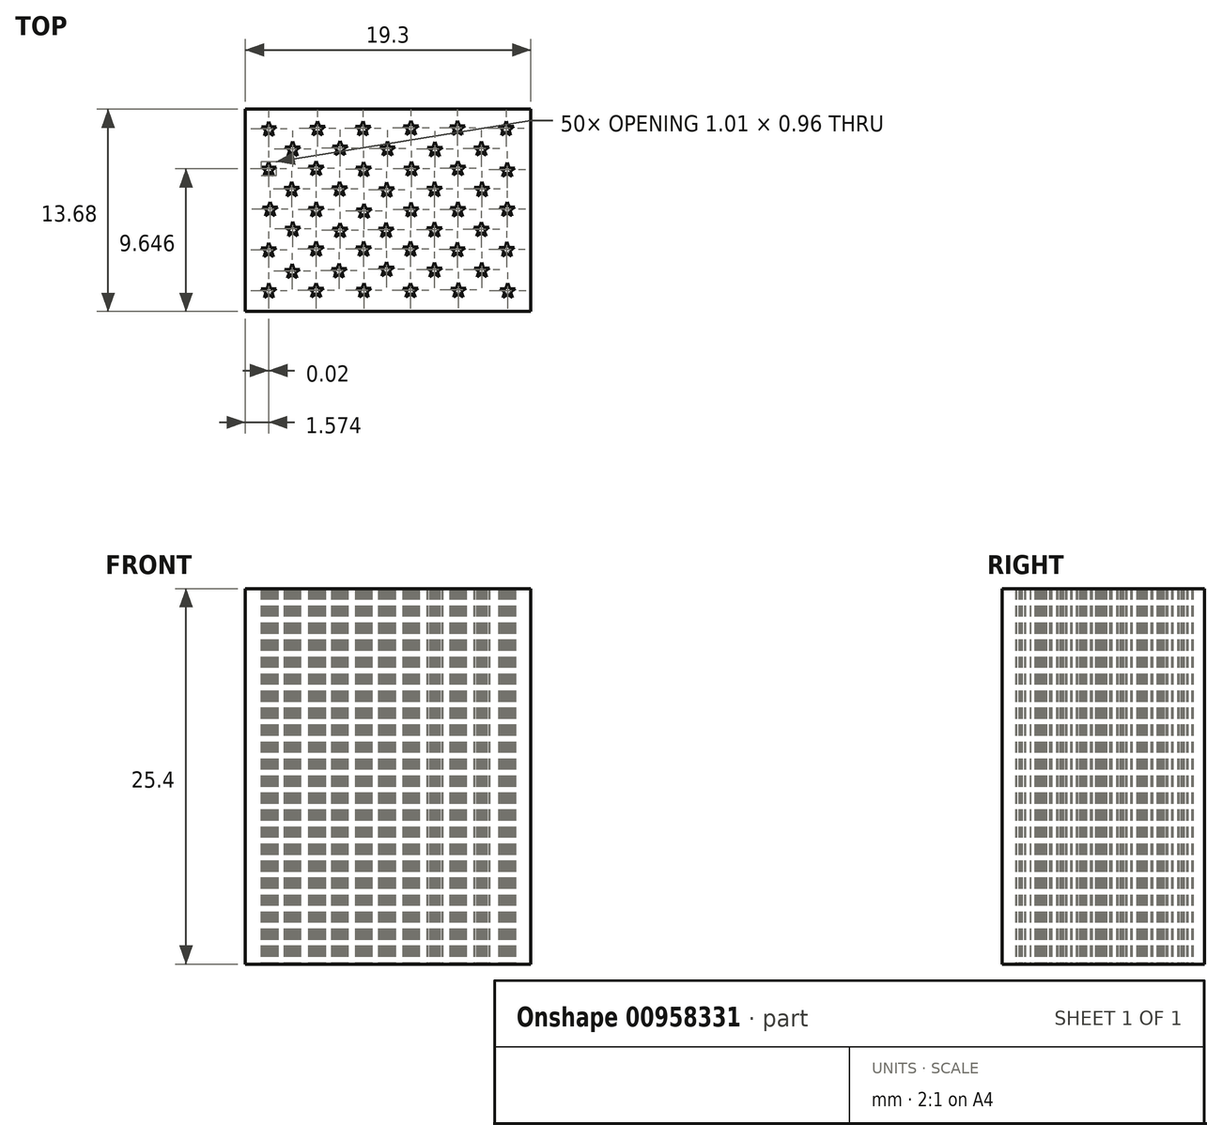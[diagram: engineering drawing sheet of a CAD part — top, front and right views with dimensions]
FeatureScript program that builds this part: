
annotation { "Feature Type Name" : "Feature", "Feature Type Description" : "" }
export const myFeature = defineFeature(function(context is Context, id is Id, definition is map)
    precondition{}
    {
        {
            var Q0;
            Q0=qCreatedBy(makeId("Top.planeOp"),FACE);
            var sketch = newSketch(context, id + "F0", { "sketchPlane" : qUnion([Q0])});
            skLineSegment(sketch, "E0", {"start": v(0, 0) * mm, "end": v(-48.26, 0) * mm});
            skLineSegment(sketch, "E1", {"start": v(-48.26, 0) * mm, "end": v(-48.26, 25.4) * mm});
            skLineSegment(sketch, "E2", {"start": v(-48.26, 25.4) * mm, "end": v(0, 25.4) * mm});
            skLineSegment(sketch, "E3", {"start": v(0, 25.4) * mm, "end": v(0, 0) * mm});
            skLineSegment(sketch, "E4", {"start": v(-49.37, -10.84) * mm, "end": v(-48.47, -27.32) * mm});
            skLineSegment(sketch, "E5", {"start": v(-49.37, -10.84) * mm, "end": v(-38.96, -23.65) * mm});
            skLineSegment(sketch, "E6", {"start": v(-23.56, -17.7) * mm, "end": v(-38.96, -23.65) * mm});
            skLineSegment(sketch, "E7", {"start": v(-47.03, -53.99) * mm, "end": v(-38.06, -40.13) * mm});
            skLineSegment(sketch, "E8.trimOffspring", {"start": v(-32.52, -31.56) * mm, "end": v(-22.11, -44.37) * mm});
            skLineSegment(sketch, "E9.trimOffspring", {"start": v(-32.52, -31.56) * mm, "end": v(-23.56, -17.7) * mm});
            skLineSegment(sketch, "E10.trimOffspring", {"start": v(-38.06, -40.13) * mm, "end": v(-22.11, -44.37) * mm});
            skLineSegment(sketch, "E11.0", {"start": v(-28.96, 23.45) * mm, "end": v(0, 23.45) * mm});
            skLineSegment(sketch, "E12.0", {"start": v(-28.96, 21.5) * mm, "end": v(0, 21.5) * mm});
            skLineSegment(sketch, "E13.0", {"start": v(-28.96, 19.54) * mm, "end": v(0, 19.54) * mm});
            skLineSegment(sketch, "E14.0", {"start": v(-28.96, 13.68) * mm, "end": v(0, 13.68) * mm});
            skLineSegment(sketch, "E15.0", {"start": v(-48.26, 11.72) * mm, "end": v(0, 11.72) * mm});
            skLineSegment(sketch, "E16.0", {"start": v(-48.26, 9.76) * mm, "end": v(0, 9.76) * mm});
            skLineSegment(sketch, "E17.0", {"start": v(-48.26, 7.8) * mm, "end": v(0, 7.8) * mm});
            skLineSegment(sketch, "E18.0", {"start": v(-48.26, 5.85) * mm, "end": v(0, 5.85) * mm});
            skLineSegment(sketch, "E19.0", {"start": v(-48.26, 3.9) * mm, "end": v(0, 3.9) * mm});
            skLineSegment(sketch, "E20.0", {"start": v(-48.26, 1.94) * mm, "end": v(0, 1.94) * mm});
            skLineSegment(sketch, "E21.0", {"start": v(-48.26, 11.7) * mm, "end": v(0, 11.7) * mm});
            skLineSegment(sketch, "E22.0", {"start": v(-46.94, 24.03) * mm, "end": v(-46.38, 24.03) * mm});
            skLineSegment(sketch, "E23", {"start": v(-47.17, 24.2) * mm, "end": v(-46.85, 23.97) * mm});
            skLineSegment(sketch, "E24", {"start": v(-46.97, 23.6) * mm, "end": v(-46.85, 23.97) * mm});
            skLineSegment(sketch, "E25", {"start": v(-46.15, 24.2) * mm, "end": v(-46.47, 23.97) * mm});
            skLineSegment(sketch, "E26", {"start": v(-46.66, 24.56) * mm, "end": v(-46.54, 24.2) * mm});
            skLineSegment(sketch, "E27", {"start": v(-47.17, 24.2) * mm, "end": v(-46.78, 24.2) * mm});
            skLineSegment(sketch, "E28.trimOffspring", {"start": v(-46.66, 23.82) * mm, "end": v(-46.97, 23.6) * mm});
            skLineSegment(sketch, "E29.trimOffspring", {"start": v(-46.47, 23.97) * mm, "end": v(-46.35, 23.6) * mm});
            skLineSegment(sketch, "E30.trimOffspring", {"start": v(-46.54, 24.2) * mm, "end": v(-46.15, 24.2) * mm});
            skLineSegment(sketch, "E31.trimOffspring", {"start": v(-46.66, 23.82) * mm, "end": v(-46.35, 23.6) * mm});
            skLineSegment(sketch, "E32.trimOffspring", {"start": v(-46.78, 24.2) * mm, "end": v(-46.66, 24.56) * mm});
            skLineSegment(sketch, "E33", {"start": v(-45.57, 22.83) * mm, "end": v(-45.25, 22.6) * mm});
            skLineSegment(sketch, "E34", {"start": v(-45.37, 22.24) * mm, "end": v(-45.25, 22.6) * mm});
            skLineSegment(sketch, "E35", {"start": v(-44.55, 22.83) * mm, "end": v(-44.87, 22.6) * mm});
            skLineSegment(sketch, "E36", {"start": v(-45.06, 23.2) * mm, "end": v(-44.94, 22.83) * mm});
            skLineSegment(sketch, "E37", {"start": v(-45.57, 22.83) * mm, "end": v(-45.18, 22.83) * mm});
            skLineSegment(sketch, "E38.trimOffspring", {"start": v(-45.06, 22.46) * mm, "end": v(-45.37, 22.24) * mm});
            skLineSegment(sketch, "E39.trimOffspring", {"start": v(-44.87, 22.6) * mm, "end": v(-44.75, 22.24) * mm});
            skLineSegment(sketch, "E40.trimOffspring", {"start": v(-44.94, 22.83) * mm, "end": v(-44.55, 22.83) * mm});
            skLineSegment(sketch, "E41.trimOffspring", {"start": v(-45.06, 22.46) * mm, "end": v(-44.75, 22.24) * mm});
            skLineSegment(sketch, "E42.trimOffspring", {"start": v(-45.18, 22.83) * mm, "end": v(-45.06, 23.2) * mm});
            skLineSegment(sketch, "E43", {"start": v(-43.89, 24.22) * mm, "end": v(-43.57, 24) * mm});
            skLineSegment(sketch, "E44", {"start": v(-43.7, 23.62) * mm, "end": v(-43.57, 24) * mm});
            skLineSegment(sketch, "E45", {"start": v(-42.87, 24.22) * mm, "end": v(-43.19, 24) * mm});
            skLineSegment(sketch, "E46", {"start": v(-43.38, 24.59) * mm, "end": v(-43.26, 24.22) * mm});
            skLineSegment(sketch, "E47", {"start": v(-43.89, 24.22) * mm, "end": v(-43.5, 24.22) * mm});
            skLineSegment(sketch, "E48.trimOffspring", {"start": v(-43.38, 23.85) * mm, "end": v(-43.7, 23.62) * mm});
            skLineSegment(sketch, "E49.trimOffspring", {"start": v(-43.19, 24) * mm, "end": v(-43.07, 23.62) * mm});
            skLineSegment(sketch, "E50.trimOffspring", {"start": v(-43.26, 24.22) * mm, "end": v(-42.87, 24.22) * mm});
            skLineSegment(sketch, "E51.trimOffspring", {"start": v(-43.38, 23.85) * mm, "end": v(-43.07, 23.62) * mm});
            skLineSegment(sketch, "E52.trimOffspring", {"start": v(-43.5, 24.22) * mm, "end": v(-43.38, 24.59) * mm});
            skLineSegment(sketch, "E53", {"start": v(-47.2, 21.48) * mm, "end": v(-46.88, 21.25) * mm});
            skLineSegment(sketch, "E54", {"start": v(-47, 20.88) * mm, "end": v(-46.88, 21.25) * mm});
            skLineSegment(sketch, "E55", {"start": v(-46.18, 21.48) * mm, "end": v(-46.5, 21.25) * mm});
            skLineSegment(sketch, "E56", {"start": v(-46.69, 21.85) * mm, "end": v(-46.57, 21.48) * mm});
            skLineSegment(sketch, "E57", {"start": v(-47.2, 21.48) * mm, "end": v(-46.8, 21.48) * mm});
            skLineSegment(sketch, "E58.trimOffspring", {"start": v(-46.69, 21.11) * mm, "end": v(-47, 20.88) * mm});
            skLineSegment(sketch, "E59.trimOffspring", {"start": v(-46.5, 21.25) * mm, "end": v(-46.37, 20.88) * mm});
            skLineSegment(sketch, "E60.trimOffspring", {"start": v(-46.57, 21.48) * mm, "end": v(-46.18, 21.48) * mm});
            skLineSegment(sketch, "E61.trimOffspring", {"start": v(-46.69, 21.11) * mm, "end": v(-46.37, 20.88) * mm});
            skLineSegment(sketch, "E62.trimOffspring", {"start": v(-46.8, 21.48) * mm, "end": v(-46.69, 21.85) * mm});
            skLineSegment(sketch, "E63", {"start": v(-45.63, 20.11) * mm, "end": v(-45.31, 19.88) * mm});
            skLineSegment(sketch, "E64", {"start": v(-45.43, 19.51) * mm, "end": v(-45.31, 19.88) * mm});
            skLineSegment(sketch, "E65", {"start": v(-44.61, 20.11) * mm, "end": v(-44.93, 19.88) * mm});
            skLineSegment(sketch, "E66", {"start": v(-45.12, 20.48) * mm, "end": v(-45, 20.11) * mm});
            skLineSegment(sketch, "E67", {"start": v(-45.63, 20.11) * mm, "end": v(-45.24, 20.11) * mm});
            skLineSegment(sketch, "E68.trimOffspring", {"start": v(-45.12, 19.74) * mm, "end": v(-45.43, 19.51) * mm});
            skLineSegment(sketch, "E69.trimOffspring", {"start": v(-44.93, 19.88) * mm, "end": v(-44.8, 19.51) * mm});
            skLineSegment(sketch, "E70.trimOffspring", {"start": v(-45, 20.11) * mm, "end": v(-44.61, 20.11) * mm});
            skLineSegment(sketch, "E71.trimOffspring", {"start": v(-45.12, 19.74) * mm, "end": v(-44.8, 19.51) * mm});
            skLineSegment(sketch, "E72.trimOffspring", {"start": v(-45.24, 20.11) * mm, "end": v(-45.12, 20.48) * mm});
            skLineSegment(sketch, "E73", {"start": v(-47.1, 18.76) * mm, "end": v(-46.78, 18.53) * mm});
            skLineSegment(sketch, "E74", {"start": v(-46.9, 18.16) * mm, "end": v(-46.78, 18.53) * mm});
            skLineSegment(sketch, "E75", {"start": v(-46.08, 18.76) * mm, "end": v(-46.4, 18.53) * mm});
            skLineSegment(sketch, "E76", {"start": v(-46.59, 19.13) * mm, "end": v(-46.47, 18.76) * mm});
            skLineSegment(sketch, "E77", {"start": v(-47.1, 18.76) * mm, "end": v(-46.7, 18.76) * mm});
            skLineSegment(sketch, "E78.trimOffspring", {"start": v(-46.59, 18.4) * mm, "end": v(-46.9, 18.16) * mm});
            skLineSegment(sketch, "E79.trimOffspring", {"start": v(-46.4, 18.53) * mm, "end": v(-46.27, 18.16) * mm});
            skLineSegment(sketch, "E80.trimOffspring", {"start": v(-46.47, 18.76) * mm, "end": v(-46.08, 18.76) * mm});
            skLineSegment(sketch, "E81.trimOffspring", {"start": v(-46.59, 18.4) * mm, "end": v(-46.27, 18.16) * mm});
            skLineSegment(sketch, "E82.trimOffspring", {"start": v(-46.7, 18.76) * mm, "end": v(-46.59, 19.13) * mm});
            skLineSegment(sketch, "E83", {"start": v(-43.97, 18.74) * mm, "end": v(-43.65, 18.51) * mm});
            skLineSegment(sketch, "E84", {"start": v(-43.77, 18.15) * mm, "end": v(-43.65, 18.51) * mm});
            skLineSegment(sketch, "E85", {"start": v(-42.95, 18.74) * mm, "end": v(-43.26, 18.51) * mm});
            skLineSegment(sketch, "E86", {"start": v(-43.46, 19.1) * mm, "end": v(-43.34, 18.74) * mm});
            skLineSegment(sketch, "E87", {"start": v(-43.97, 18.74) * mm, "end": v(-43.58, 18.74) * mm});
            skLineSegment(sketch, "E88.trimOffspring", {"start": v(-43.46, 18.37) * mm, "end": v(-43.77, 18.15) * mm});
            skLineSegment(sketch, "E89.trimOffspring", {"start": v(-43.26, 18.51) * mm, "end": v(-43.14, 18.15) * mm});
            skLineSegment(sketch, "E90.trimOffspring", {"start": v(-43.34, 18.74) * mm, "end": v(-42.95, 18.74) * mm});
            skLineSegment(sketch, "E91.trimOffspring", {"start": v(-43.46, 18.37) * mm, "end": v(-43.14, 18.15) * mm});
            skLineSegment(sketch, "E92.trimOffspring", {"start": v(-43.58, 18.74) * mm, "end": v(-43.46, 19.1) * mm});
            skLineSegment(sketch, "E93", {"start": v(-43.98, 21.52) * mm, "end": v(-43.67, 21.3) * mm});
            skLineSegment(sketch, "E94", {"start": v(-43.8, 20.92) * mm, "end": v(-43.67, 21.3) * mm});
            skLineSegment(sketch, "E95", {"start": v(-42.97, 21.52) * mm, "end": v(-43.28, 21.3) * mm});
            skLineSegment(sketch, "E96", {"start": v(-43.48, 21.89) * mm, "end": v(-43.36, 21.52) * mm});
            skLineSegment(sketch, "E97", {"start": v(-43.98, 21.52) * mm, "end": v(-43.6, 21.52) * mm});
            skLineSegment(sketch, "E98.trimOffspring", {"start": v(-43.48, 21.15) * mm, "end": v(-43.8, 20.92) * mm});
            skLineSegment(sketch, "E99.trimOffspring", {"start": v(-43.28, 21.3) * mm, "end": v(-43.16, 20.92) * mm});
            skLineSegment(sketch, "E100.trimOffspring", {"start": v(-43.36, 21.52) * mm, "end": v(-42.97, 21.52) * mm});
            skLineSegment(sketch, "E101.trimOffspring", {"start": v(-43.48, 21.15) * mm, "end": v(-43.16, 20.92) * mm});
            skLineSegment(sketch, "E102.trimOffspring", {"start": v(-43.6, 21.52) * mm, "end": v(-43.48, 21.89) * mm});
            skLineSegment(sketch, "E103", {"start": v(-42.36, 22.89) * mm, "end": v(-42.05, 22.66) * mm});
            skLineSegment(sketch, "E104", {"start": v(-42.17, 22.3) * mm, "end": v(-42.05, 22.66) * mm});
            skLineSegment(sketch, "E105", {"start": v(-41.35, 22.89) * mm, "end": v(-41.66, 22.66) * mm});
            skLineSegment(sketch, "E106", {"start": v(-41.85, 23.26) * mm, "end": v(-41.73, 22.89) * mm});
            skLineSegment(sketch, "E107", {"start": v(-42.36, 22.89) * mm, "end": v(-41.97, 22.89) * mm});
            skLineSegment(sketch, "E108.trimOffspring", {"start": v(-41.85, 22.52) * mm, "end": v(-42.17, 22.3) * mm});
            skLineSegment(sketch, "E109.trimOffspring", {"start": v(-41.66, 22.66) * mm, "end": v(-41.54, 22.3) * mm});
            skLineSegment(sketch, "E110.trimOffspring", {"start": v(-41.73, 22.89) * mm, "end": v(-41.35, 22.89) * mm});
            skLineSegment(sketch, "E111.trimOffspring", {"start": v(-41.85, 22.52) * mm, "end": v(-41.54, 22.3) * mm});
            skLineSegment(sketch, "E112.trimOffspring", {"start": v(-41.97, 22.89) * mm, "end": v(-41.85, 23.26) * mm});
            skLineSegment(sketch, "E113", {"start": v(-42.38, 20.13) * mm, "end": v(-42.07, 19.9) * mm});
            skLineSegment(sketch, "E114", {"start": v(-42.19, 19.53) * mm, "end": v(-42.07, 19.9) * mm});
            skLineSegment(sketch, "E115", {"start": v(-41.37, 20.13) * mm, "end": v(-41.68, 19.9) * mm});
            skLineSegment(sketch, "E116", {"start": v(-41.87, 20.5) * mm, "end": v(-41.75, 20.13) * mm});
            skLineSegment(sketch, "E117", {"start": v(-42.38, 20.13) * mm, "end": v(-42, 20.13) * mm});
            skLineSegment(sketch, "E118.trimOffspring", {"start": v(-41.87, 19.76) * mm, "end": v(-42.19, 19.53) * mm});
            skLineSegment(sketch, "E119.trimOffspring", {"start": v(-41.68, 19.9) * mm, "end": v(-41.56, 19.53) * mm});
            skLineSegment(sketch, "E120.trimOffspring", {"start": v(-41.75, 20.13) * mm, "end": v(-41.37, 20.13) * mm});
            skLineSegment(sketch, "E121.trimOffspring", {"start": v(-41.87, 19.76) * mm, "end": v(-41.56, 19.53) * mm});
            skLineSegment(sketch, "E122.trimOffspring", {"start": v(-42, 20.13) * mm, "end": v(-41.87, 20.5) * mm});
            skLineSegment(sketch, "E123", {"start": v(-40.76, 21.46) * mm, "end": v(-40.44, 21.23) * mm});
            skLineSegment(sketch, "E124", {"start": v(-40.56, 20.86) * mm, "end": v(-40.44, 21.23) * mm});
            skLineSegment(sketch, "E125", {"start": v(-39.74, 21.46) * mm, "end": v(-40.06, 21.23) * mm});
            skLineSegment(sketch, "E126", {"start": v(-40.25, 21.83) * mm, "end": v(-40.13, 21.46) * mm});
            skLineSegment(sketch, "E127", {"start": v(-40.76, 21.46) * mm, "end": v(-40.37, 21.46) * mm});
            skLineSegment(sketch, "E128.trimOffspring", {"start": v(-40.25, 21.1) * mm, "end": v(-40.56, 20.86) * mm});
            skLineSegment(sketch, "E129.trimOffspring", {"start": v(-40.06, 21.23) * mm, "end": v(-39.94, 20.86) * mm});
            skLineSegment(sketch, "E130.trimOffspring", {"start": v(-40.13, 21.46) * mm, "end": v(-39.74, 21.46) * mm});
            skLineSegment(sketch, "E131.trimOffspring", {"start": v(-40.25, 21.1) * mm, "end": v(-39.94, 20.86) * mm});
            skLineSegment(sketch, "E132.trimOffspring", {"start": v(-40.37, 21.46) * mm, "end": v(-40.25, 21.83) * mm});
            skLineSegment(sketch, "E133", {"start": v(-45.55, 17.41) * mm, "end": v(-45.24, 17.18) * mm});
            skLineSegment(sketch, "E134", {"start": v(-45.36, 16.82) * mm, "end": v(-45.24, 17.18) * mm});
            skLineSegment(sketch, "E135", {"start": v(-44.54, 17.41) * mm, "end": v(-44.85, 17.18) * mm});
            skLineSegment(sketch, "E136", {"start": v(-45.04, 17.78) * mm, "end": v(-44.92, 17.41) * mm});
            skLineSegment(sketch, "E137", {"start": v(-45.55, 17.41) * mm, "end": v(-45.16, 17.41) * mm});
            skLineSegment(sketch, "E138.trimOffspring", {"start": v(-45.04, 17.04) * mm, "end": v(-45.36, 16.82) * mm});
            skLineSegment(sketch, "E139.trimOffspring", {"start": v(-44.85, 17.18) * mm, "end": v(-44.73, 16.82) * mm});
            skLineSegment(sketch, "E140.trimOffspring", {"start": v(-44.92, 17.41) * mm, "end": v(-44.54, 17.41) * mm});
            skLineSegment(sketch, "E141.trimOffspring", {"start": v(-45.04, 17.04) * mm, "end": v(-44.73, 16.82) * mm});
            skLineSegment(sketch, "E142.trimOffspring", {"start": v(-45.16, 17.41) * mm, "end": v(-45.04, 17.78) * mm});
            skLineSegment(sketch, "E143", {"start": v(-47.17, 16) * mm, "end": v(-46.86, 15.78) * mm});
            skLineSegment(sketch, "E144", {"start": v(-46.98, 15.4) * mm, "end": v(-46.86, 15.78) * mm});
            skLineSegment(sketch, "E145", {"start": v(-46.16, 16) * mm, "end": v(-46.47, 15.78) * mm});
            skLineSegment(sketch, "E146", {"start": v(-46.67, 16.37) * mm, "end": v(-46.55, 16) * mm});
            skLineSegment(sketch, "E147", {"start": v(-47.17, 16) * mm, "end": v(-46.79, 16) * mm});
            skLineSegment(sketch, "E148.trimOffspring", {"start": v(-46.67, 15.63) * mm, "end": v(-46.98, 15.4) * mm});
            skLineSegment(sketch, "E149.trimOffspring", {"start": v(-46.47, 15.78) * mm, "end": v(-46.35, 15.4) * mm});
            skLineSegment(sketch, "E150.trimOffspring", {"start": v(-46.55, 16) * mm, "end": v(-46.16, 16) * mm});
            skLineSegment(sketch, "E151.trimOffspring", {"start": v(-46.67, 15.63) * mm, "end": v(-46.35, 15.4) * mm});
            skLineSegment(sketch, "E152.trimOffspring", {"start": v(-46.79, 16) * mm, "end": v(-46.67, 16.37) * mm});
            skLineSegment(sketch, "E153", {"start": v(-39.15, 22.85) * mm, "end": v(-38.84, 22.62) * mm});
            skLineSegment(sketch, "E154", {"start": v(-38.96, 22.25) * mm, "end": v(-38.84, 22.62) * mm});
            skLineSegment(sketch, "E155", {"start": v(-38.14, 22.85) * mm, "end": v(-38.45, 22.62) * mm});
            skLineSegment(sketch, "E156", {"start": v(-38.65, 23.22) * mm, "end": v(-38.53, 22.85) * mm});
            skLineSegment(sketch, "E157", {"start": v(-39.15, 22.85) * mm, "end": v(-38.77, 22.85) * mm});
            skLineSegment(sketch, "E158.trimOffspring", {"start": v(-38.65, 22.48) * mm, "end": v(-38.96, 22.25) * mm});
            skLineSegment(sketch, "E159.trimOffspring", {"start": v(-38.45, 22.62) * mm, "end": v(-38.33, 22.25) * mm});
            skLineSegment(sketch, "E160.trimOffspring", {"start": v(-38.53, 22.85) * mm, "end": v(-38.14, 22.85) * mm});
            skLineSegment(sketch, "E161.trimOffspring", {"start": v(-38.65, 22.48) * mm, "end": v(-38.33, 22.25) * mm});
            skLineSegment(sketch, "E162.trimOffspring", {"start": v(-38.77, 22.85) * mm, "end": v(-38.65, 23.22) * mm});
            skLineSegment(sketch, "E163", {"start": v(-37.57, 24.26) * mm, "end": v(-37.25, 24.03) * mm});
            skLineSegment(sketch, "E164", {"start": v(-37.37, 23.66) * mm, "end": v(-37.25, 24.03) * mm});
            skLineSegment(sketch, "E165", {"start": v(-36.55, 24.26) * mm, "end": v(-36.87, 24.03) * mm});
            skLineSegment(sketch, "E166", {"start": v(-37.06, 24.63) * mm, "end": v(-36.94, 24.26) * mm});
            skLineSegment(sketch, "E167", {"start": v(-37.57, 24.26) * mm, "end": v(-37.18, 24.26) * mm});
            skLineSegment(sketch, "E168.trimOffspring", {"start": v(-37.06, 23.89) * mm, "end": v(-37.37, 23.66) * mm});
            skLineSegment(sketch, "E169.trimOffspring", {"start": v(-36.87, 24.03) * mm, "end": v(-36.75, 23.66) * mm});
            skLineSegment(sketch, "E170.trimOffspring", {"start": v(-36.94, 24.26) * mm, "end": v(-36.55, 24.26) * mm});
            skLineSegment(sketch, "E171.trimOffspring", {"start": v(-37.06, 23.89) * mm, "end": v(-36.75, 23.66) * mm});
            skLineSegment(sketch, "E172.trimOffspring", {"start": v(-37.18, 24.26) * mm, "end": v(-37.06, 24.63) * mm});
            skLineSegment(sketch, "E173", {"start": v(-40.82, 24.22) * mm, "end": v(-40.5, 24) * mm});
            skLineSegment(sketch, "E174", {"start": v(-40.62, 23.62) * mm, "end": v(-40.5, 24) * mm});
            skLineSegment(sketch, "E175", {"start": v(-39.8, 24.22) * mm, "end": v(-40.11, 24) * mm});
            skLineSegment(sketch, "E176", {"start": v(-40.3, 24.59) * mm, "end": v(-40.19, 24.22) * mm});
            skLineSegment(sketch, "E177", {"start": v(-40.82, 24.22) * mm, "end": v(-40.43, 24.22) * mm});
            skLineSegment(sketch, "E178.trimOffspring", {"start": v(-40.3, 23.85) * mm, "end": v(-40.62, 23.62) * mm});
            skLineSegment(sketch, "E179.trimOffspring", {"start": v(-40.11, 24) * mm, "end": v(-40, 23.62) * mm});
            skLineSegment(sketch, "E180.trimOffspring", {"start": v(-40.19, 24.22) * mm, "end": v(-39.8, 24.22) * mm});
            skLineSegment(sketch, "E181.trimOffspring", {"start": v(-40.3, 23.85) * mm, "end": v(-40, 23.62) * mm});
            skLineSegment(sketch, "E182.trimOffspring", {"start": v(-40.43, 24.22) * mm, "end": v(-40.3, 24.59) * mm});
            skLineSegment(sketch, "E183", {"start": v(-35.94, 22.81) * mm, "end": v(-35.63, 22.58) * mm});
            skLineSegment(sketch, "E184", {"start": v(-35.75, 22.21) * mm, "end": v(-35.63, 22.58) * mm});
            skLineSegment(sketch, "E185", {"start": v(-34.93, 22.81) * mm, "end": v(-35.24, 22.58) * mm});
            skLineSegment(sketch, "E186", {"start": v(-35.44, 23.18) * mm, "end": v(-35.32, 22.81) * mm});
            skLineSegment(sketch, "E187", {"start": v(-35.94, 22.81) * mm, "end": v(-35.56, 22.81) * mm});
            skLineSegment(sketch, "E188.trimOffspring", {"start": v(-35.44, 22.44) * mm, "end": v(-35.75, 22.21) * mm});
            skLineSegment(sketch, "E189.trimOffspring", {"start": v(-35.24, 22.58) * mm, "end": v(-35.12, 22.21) * mm});
            skLineSegment(sketch, "E190.trimOffspring", {"start": v(-35.32, 22.81) * mm, "end": v(-34.93, 22.81) * mm});
            skLineSegment(sketch, "E191.trimOffspring", {"start": v(-35.44, 22.44) * mm, "end": v(-35.12, 22.21) * mm});
            skLineSegment(sketch, "E192.trimOffspring", {"start": v(-35.56, 22.81) * mm, "end": v(-35.44, 23.18) * mm});
            skLineSegment(sketch, "E193", {"start": v(-34.38, 21.52) * mm, "end": v(-34.07, 21.3) * mm});
            skLineSegment(sketch, "E194", {"start": v(-34.19, 20.92) * mm, "end": v(-34.07, 21.3) * mm});
            skLineSegment(sketch, "E195", {"start": v(-33.36, 21.52) * mm, "end": v(-33.68, 21.3) * mm});
            skLineSegment(sketch, "E196", {"start": v(-33.87, 21.89) * mm, "end": v(-33.75, 21.52) * mm});
            skLineSegment(sketch, "E197", {"start": v(-34.38, 21.52) * mm, "end": v(-34, 21.52) * mm});
            skLineSegment(sketch, "E198.trimOffspring", {"start": v(-33.87, 21.15) * mm, "end": v(-34.19, 20.92) * mm});
            skLineSegment(sketch, "E199.trimOffspring", {"start": v(-33.68, 21.3) * mm, "end": v(-33.56, 20.92) * mm});
            skLineSegment(sketch, "E200.trimOffspring", {"start": v(-33.75, 21.52) * mm, "end": v(-33.36, 21.52) * mm});
            skLineSegment(sketch, "E201.trimOffspring", {"start": v(-33.87, 21.15) * mm, "end": v(-33.56, 20.92) * mm});
            skLineSegment(sketch, "E202.trimOffspring", {"start": v(-34, 21.52) * mm, "end": v(-33.87, 21.89) * mm});
            skLineSegment(sketch, "E203", {"start": v(-32.76, 20.11) * mm, "end": v(-32.44, 19.88) * mm});
            skLineSegment(sketch, "E204", {"start": v(-32.56, 19.51) * mm, "end": v(-32.44, 19.88) * mm});
            skLineSegment(sketch, "E205", {"start": v(-31.74, 20.11) * mm, "end": v(-32.05, 19.88) * mm});
            skLineSegment(sketch, "E206", {"start": v(-32.25, 20.48) * mm, "end": v(-32.13, 20.11) * mm});
            skLineSegment(sketch, "E207", {"start": v(-32.76, 20.11) * mm, "end": v(-32.37, 20.11) * mm});
            skLineSegment(sketch, "E208.trimOffspring", {"start": v(-32.25, 19.74) * mm, "end": v(-32.56, 19.51) * mm});
            skLineSegment(sketch, "E209.trimOffspring", {"start": v(-32.05, 19.88) * mm, "end": v(-31.93, 19.51) * mm});
            skLineSegment(sketch, "E210.trimOffspring", {"start": v(-32.13, 20.11) * mm, "end": v(-31.74, 20.11) * mm});
            skLineSegment(sketch, "E211.trimOffspring", {"start": v(-32.25, 19.74) * mm, "end": v(-31.93, 19.51) * mm});
            skLineSegment(sketch, "E212.trimOffspring", {"start": v(-32.37, 20.11) * mm, "end": v(-32.25, 20.48) * mm});
            skLineSegment(sketch, "E213", {"start": v(-31.05, 18.76) * mm, "end": v(-30.74, 18.53) * mm});
            skLineSegment(sketch, "E214", {"start": v(-30.86, 18.16) * mm, "end": v(-30.74, 18.53) * mm});
            skLineSegment(sketch, "E215", {"start": v(-30.04, 18.76) * mm, "end": v(-30.35, 18.53) * mm});
            skLineSegment(sketch, "E216", {"start": v(-30.55, 19.13) * mm, "end": v(-30.43, 18.76) * mm});
            skLineSegment(sketch, "E217", {"start": v(-31.05, 18.76) * mm, "end": v(-30.67, 18.76) * mm});
            skLineSegment(sketch, "E218.trimOffspring", {"start": v(-30.55, 18.4) * mm, "end": v(-30.86, 18.16) * mm});
            skLineSegment(sketch, "E219.trimOffspring", {"start": v(-30.35, 18.53) * mm, "end": v(-30.23, 18.16) * mm});
            skLineSegment(sketch, "E220.trimOffspring", {"start": v(-30.43, 18.76) * mm, "end": v(-30.04, 18.76) * mm});
            skLineSegment(sketch, "E221.trimOffspring", {"start": v(-30.55, 18.4) * mm, "end": v(-30.23, 18.16) * mm});
            skLineSegment(sketch, "E222.trimOffspring", {"start": v(-30.67, 18.76) * mm, "end": v(-30.55, 19.13) * mm});
            skLineSegment(sketch, "E223", {"start": v(-37.53, 21.48) * mm, "end": v(-37.22, 21.25) * mm});
            skLineSegment(sketch, "E224", {"start": v(-37.34, 20.88) * mm, "end": v(-37.22, 21.25) * mm});
            skLineSegment(sketch, "E225", {"start": v(-36.51, 21.48) * mm, "end": v(-36.83, 21.25) * mm});
            skLineSegment(sketch, "E226", {"start": v(-37.02, 21.85) * mm, "end": v(-36.9, 21.48) * mm});
            skLineSegment(sketch, "E227", {"start": v(-37.53, 21.48) * mm, "end": v(-37.14, 21.48) * mm});
            skLineSegment(sketch, "E228.trimOffspring", {"start": v(-37.02, 21.11) * mm, "end": v(-37.34, 20.88) * mm});
            skLineSegment(sketch, "E229.trimOffspring", {"start": v(-36.83, 21.25) * mm, "end": v(-36.7, 20.88) * mm});
            skLineSegment(sketch, "E230.trimOffspring", {"start": v(-36.9, 21.48) * mm, "end": v(-36.51, 21.48) * mm});
            skLineSegment(sketch, "E231.trimOffspring", {"start": v(-37.02, 21.11) * mm, "end": v(-36.7, 20.88) * mm});
            skLineSegment(sketch, "E232.trimOffspring", {"start": v(-37.14, 21.48) * mm, "end": v(-37.02, 21.85) * mm});
            skLineSegment(sketch, "E233", {"start": v(-35.96, 20.11) * mm, "end": v(-35.65, 19.88) * mm});
            skLineSegment(sketch, "E234", {"start": v(-35.77, 19.51) * mm, "end": v(-35.65, 19.88) * mm});
            skLineSegment(sketch, "E235", {"start": v(-34.95, 20.11) * mm, "end": v(-35.26, 19.88) * mm});
            skLineSegment(sketch, "E236", {"start": v(-35.46, 20.48) * mm, "end": v(-35.34, 20.11) * mm});
            skLineSegment(sketch, "E237", {"start": v(-35.96, 20.11) * mm, "end": v(-35.58, 20.11) * mm});
            skLineSegment(sketch, "E238.trimOffspring", {"start": v(-35.46, 19.74) * mm, "end": v(-35.77, 19.51) * mm});
            skLineSegment(sketch, "E239.trimOffspring", {"start": v(-35.26, 19.88) * mm, "end": v(-35.14, 19.51) * mm});
            skLineSegment(sketch, "E240.trimOffspring", {"start": v(-35.34, 20.11) * mm, "end": v(-34.95, 20.11) * mm});
            skLineSegment(sketch, "E241.trimOffspring", {"start": v(-35.46, 19.74) * mm, "end": v(-35.14, 19.51) * mm});
            skLineSegment(sketch, "E242.trimOffspring", {"start": v(-35.58, 20.11) * mm, "end": v(-35.46, 20.48) * mm});
            skLineSegment(sketch, "E243", {"start": v(-34.38, 18.74) * mm, "end": v(-34.07, 18.51) * mm});
            skLineSegment(sketch, "E244", {"start": v(-34.19, 18.15) * mm, "end": v(-34.07, 18.51) * mm});
            skLineSegment(sketch, "E245", {"start": v(-33.36, 18.74) * mm, "end": v(-33.68, 18.51) * mm});
            skLineSegment(sketch, "E246", {"start": v(-33.87, 19.1) * mm, "end": v(-33.75, 18.74) * mm});
            skLineSegment(sketch, "E247", {"start": v(-34.38, 18.74) * mm, "end": v(-34, 18.74) * mm});
            skLineSegment(sketch, "E248.trimOffspring", {"start": v(-33.87, 18.37) * mm, "end": v(-34.19, 18.15) * mm});
            skLineSegment(sketch, "E249.trimOffspring", {"start": v(-33.68, 18.51) * mm, "end": v(-33.56, 18.15) * mm});
            skLineSegment(sketch, "E250.trimOffspring", {"start": v(-33.75, 18.74) * mm, "end": v(-33.36, 18.74) * mm});
            skLineSegment(sketch, "E251.trimOffspring", {"start": v(-33.87, 18.37) * mm, "end": v(-33.56, 18.15) * mm});
            skLineSegment(sketch, "E252.trimOffspring", {"start": v(-34, 18.74) * mm, "end": v(-33.87, 19.1) * mm});
            skLineSegment(sketch, "E253", {"start": v(-32.8, 17.4) * mm, "end": v(-32.48, 17.16) * mm});
            skLineSegment(sketch, "E254", {"start": v(-32.6, 16.8) * mm, "end": v(-32.48, 17.16) * mm});
            skLineSegment(sketch, "E255", {"start": v(-31.78, 17.4) * mm, "end": v(-32.1, 17.16) * mm});
            skLineSegment(sketch, "E256", {"start": v(-32.29, 17.76) * mm, "end": v(-32.17, 17.4) * mm});
            skLineSegment(sketch, "E257", {"start": v(-32.8, 17.4) * mm, "end": v(-32.4, 17.4) * mm});
            skLineSegment(sketch, "E258.trimOffspring", {"start": v(-32.29, 17.02) * mm, "end": v(-32.6, 16.8) * mm});
            skLineSegment(sketch, "E259.trimOffspring", {"start": v(-32.1, 17.16) * mm, "end": v(-31.97, 16.8) * mm});
            skLineSegment(sketch, "E260.trimOffspring", {"start": v(-32.17, 17.4) * mm, "end": v(-31.78, 17.4) * mm});
            skLineSegment(sketch, "E261.trimOffspring", {"start": v(-32.29, 17.02) * mm, "end": v(-31.97, 16.8) * mm});
            skLineSegment(sketch, "E262.trimOffspring", {"start": v(-32.4, 17.4) * mm, "end": v(-32.29, 17.76) * mm});
            skLineSegment(sketch, "E263", {"start": v(-31.07, 16.04) * mm, "end": v(-30.76, 15.81) * mm});
            skLineSegment(sketch, "E264", {"start": v(-30.88, 15.45) * mm, "end": v(-30.76, 15.81) * mm});
            skLineSegment(sketch, "E265", {"start": v(-30.06, 16.04) * mm, "end": v(-30.37, 15.81) * mm});
            skLineSegment(sketch, "E266", {"start": v(-30.57, 16.41) * mm, "end": v(-30.45, 16.04) * mm});
            skLineSegment(sketch, "E267", {"start": v(-31.07, 16.04) * mm, "end": v(-30.69, 16.04) * mm});
            skLineSegment(sketch, "E268.trimOffspring", {"start": v(-30.57, 15.67) * mm, "end": v(-30.88, 15.45) * mm});
            skLineSegment(sketch, "E269.trimOffspring", {"start": v(-30.37, 15.81) * mm, "end": v(-30.25, 15.45) * mm});
            skLineSegment(sketch, "E270.trimOffspring", {"start": v(-30.45, 16.04) * mm, "end": v(-30.06, 16.04) * mm});
            skLineSegment(sketch, "E271.trimOffspring", {"start": v(-30.57, 15.67) * mm, "end": v(-30.25, 15.45) * mm});
            skLineSegment(sketch, "E272.trimOffspring", {"start": v(-30.69, 16.04) * mm, "end": v(-30.57, 16.41) * mm});
            skLineSegment(sketch, "E273", {"start": v(-31.05, 21.42) * mm, "end": v(-30.74, 21.2) * mm});
            skLineSegment(sketch, "E274", {"start": v(-30.86, 20.83) * mm, "end": v(-30.74, 21.2) * mm});
            skLineSegment(sketch, "E275", {"start": v(-30.04, 21.42) * mm, "end": v(-30.35, 21.2) * mm});
            skLineSegment(sketch, "E276", {"start": v(-30.55, 21.79) * mm, "end": v(-30.43, 21.42) * mm});
            skLineSegment(sketch, "E277", {"start": v(-31.05, 21.42) * mm, "end": v(-30.67, 21.42) * mm});
            skLineSegment(sketch, "E278.trimOffspring", {"start": v(-30.55, 21.05) * mm, "end": v(-30.86, 20.83) * mm});
            skLineSegment(sketch, "E279.trimOffspring", {"start": v(-30.35, 21.2) * mm, "end": v(-30.23, 20.83) * mm});
            skLineSegment(sketch, "E280.trimOffspring", {"start": v(-30.43, 21.42) * mm, "end": v(-30.04, 21.42) * mm});
            skLineSegment(sketch, "E281.trimOffspring", {"start": v(-30.55, 21.05) * mm, "end": v(-30.23, 20.83) * mm});
            skLineSegment(sketch, "E282.trimOffspring", {"start": v(-30.67, 21.42) * mm, "end": v(-30.55, 21.79) * mm});
            skLineSegment(sketch, "E283", {"start": v(-31.13, 24.22) * mm, "end": v(-30.82, 24) * mm});
            skLineSegment(sketch, "E284", {"start": v(-30.94, 23.62) * mm, "end": v(-30.82, 24) * mm});
            skLineSegment(sketch, "E285", {"start": v(-30.12, 24.22) * mm, "end": v(-30.43, 24) * mm});
            skLineSegment(sketch, "E286", {"start": v(-30.62, 24.59) * mm, "end": v(-30.5, 24.22) * mm});
            skLineSegment(sketch, "E287", {"start": v(-31.13, 24.22) * mm, "end": v(-30.74, 24.22) * mm});
            skLineSegment(sketch, "E288.trimOffspring", {"start": v(-30.62, 23.85) * mm, "end": v(-30.94, 23.62) * mm});
            skLineSegment(sketch, "E289.trimOffspring", {"start": v(-30.43, 24) * mm, "end": v(-30.31, 23.62) * mm});
            skLineSegment(sketch, "E290.trimOffspring", {"start": v(-30.5, 24.22) * mm, "end": v(-30.12, 24.22) * mm});
            skLineSegment(sketch, "E291.trimOffspring", {"start": v(-30.62, 23.85) * mm, "end": v(-30.31, 23.62) * mm});
            skLineSegment(sketch, "E292.trimOffspring", {"start": v(-30.74, 24.22) * mm, "end": v(-30.62, 24.59) * mm});
            skLineSegment(sketch, "E293", {"start": v(-32.8, 22.85) * mm, "end": v(-32.48, 22.62) * mm});
            skLineSegment(sketch, "E294", {"start": v(-32.6, 22.25) * mm, "end": v(-32.48, 22.62) * mm});
            skLineSegment(sketch, "E295", {"start": v(-31.78, 22.85) * mm, "end": v(-32.1, 22.62) * mm});
            skLineSegment(sketch, "E296", {"start": v(-32.29, 23.22) * mm, "end": v(-32.17, 22.85) * mm});
            skLineSegment(sketch, "E297", {"start": v(-32.8, 22.85) * mm, "end": v(-32.4, 22.85) * mm});
            skLineSegment(sketch, "E298.trimOffspring", {"start": v(-32.29, 22.48) * mm, "end": v(-32.6, 22.25) * mm});
            skLineSegment(sketch, "E299.trimOffspring", {"start": v(-32.1, 22.62) * mm, "end": v(-31.97, 22.25) * mm});
            skLineSegment(sketch, "E300.trimOffspring", {"start": v(-32.17, 22.85) * mm, "end": v(-31.78, 22.85) * mm});
            skLineSegment(sketch, "E301.trimOffspring", {"start": v(-32.29, 22.48) * mm, "end": v(-31.97, 22.25) * mm});
            skLineSegment(sketch, "E302.trimOffspring", {"start": v(-32.4, 22.85) * mm, "end": v(-32.29, 23.22) * mm});
            skLineSegment(sketch, "E303", {"start": v(-34.4, 24.26) * mm, "end": v(-34.1, 24.03) * mm});
            skLineSegment(sketch, "E304", {"start": v(-34.21, 23.66) * mm, "end": v(-34.1, 24.03) * mm});
            skLineSegment(sketch, "E305", {"start": v(-33.4, 24.26) * mm, "end": v(-33.7, 24.03) * mm});
            skLineSegment(sketch, "E306", {"start": v(-33.9, 24.63) * mm, "end": v(-33.78, 24.26) * mm});
            skLineSegment(sketch, "E307", {"start": v(-34.4, 24.26) * mm, "end": v(-34.02, 24.26) * mm});
            skLineSegment(sketch, "E308.trimOffspring", {"start": v(-33.9, 23.89) * mm, "end": v(-34.21, 23.66) * mm});
            skLineSegment(sketch, "E309.trimOffspring", {"start": v(-33.7, 24.03) * mm, "end": v(-33.59, 23.66) * mm});
            skLineSegment(sketch, "E310.trimOffspring", {"start": v(-33.78, 24.26) * mm, "end": v(-33.4, 24.26) * mm});
            skLineSegment(sketch, "E311.trimOffspring", {"start": v(-33.9, 23.89) * mm, "end": v(-33.59, 23.66) * mm});
            skLineSegment(sketch, "E312.trimOffspring", {"start": v(-34.02, 24.26) * mm, "end": v(-33.9, 24.63) * mm});
            skLineSegment(sketch, "E313", {"start": v(-39.2, 20.07) * mm, "end": v(-38.89, 19.84) * mm});
            skLineSegment(sketch, "E314", {"start": v(-39, 19.47) * mm, "end": v(-38.89, 19.84) * mm});
            skLineSegment(sketch, "E315", {"start": v(-38.19, 20.07) * mm, "end": v(-38.5, 19.84) * mm});
            skLineSegment(sketch, "E316", {"start": v(-38.7, 20.44) * mm, "end": v(-38.57, 20.07) * mm});
            skLineSegment(sketch, "E317", {"start": v(-39.2, 20.07) * mm, "end": v(-38.81, 20.07) * mm});
            skLineSegment(sketch, "E318.trimOffspring", {"start": v(-38.7, 19.7) * mm, "end": v(-39, 19.47) * mm});
            skLineSegment(sketch, "E319.trimOffspring", {"start": v(-38.5, 19.84) * mm, "end": v(-38.38, 19.47) * mm});
            skLineSegment(sketch, "E320.trimOffspring", {"start": v(-38.57, 20.07) * mm, "end": v(-38.19, 20.07) * mm});
            skLineSegment(sketch, "E321.trimOffspring", {"start": v(-38.7, 19.7) * mm, "end": v(-38.38, 19.47) * mm});
            skLineSegment(sketch, "E322.trimOffspring", {"start": v(-38.81, 20.07) * mm, "end": v(-38.7, 20.44) * mm});
            skLineSegment(sketch, "E323", {"start": v(-39.25, 17.35) * mm, "end": v(-38.93, 17.12) * mm});
            skLineSegment(sketch, "E324", {"start": v(-39.05, 16.75) * mm, "end": v(-38.93, 17.12) * mm});
            skLineSegment(sketch, "E325", {"start": v(-38.23, 17.35) * mm, "end": v(-38.55, 17.12) * mm});
            skLineSegment(sketch, "E326", {"start": v(-38.74, 17.72) * mm, "end": v(-38.62, 17.35) * mm});
            skLineSegment(sketch, "E327", {"start": v(-39.25, 17.35) * mm, "end": v(-38.86, 17.35) * mm});
            skLineSegment(sketch, "E328.trimOffspring", {"start": v(-38.74, 16.98) * mm, "end": v(-39.05, 16.75) * mm});
            skLineSegment(sketch, "E329.trimOffspring", {"start": v(-38.55, 17.12) * mm, "end": v(-38.43, 16.75) * mm});
            skLineSegment(sketch, "E330.trimOffspring", {"start": v(-38.62, 17.35) * mm, "end": v(-38.23, 17.35) * mm});
            skLineSegment(sketch, "E331.trimOffspring", {"start": v(-38.74, 16.98) * mm, "end": v(-38.43, 16.75) * mm});
            skLineSegment(sketch, "E332.trimOffspring", {"start": v(-38.86, 17.35) * mm, "end": v(-38.74, 17.72) * mm});
            skLineSegment(sketch, "E333", {"start": v(-39.22, 14.7) * mm, "end": v(-38.91, 14.47) * mm});
            skLineSegment(sketch, "E334", {"start": v(-39.03, 14.1) * mm, "end": v(-38.91, 14.47) * mm});
            skLineSegment(sketch, "E335", {"start": v(-38.2, 14.7) * mm, "end": v(-38.52, 14.47) * mm});
            skLineSegment(sketch, "E336", {"start": v(-38.72, 15.07) * mm, "end": v(-38.6, 14.7) * mm});
            skLineSegment(sketch, "E337", {"start": v(-39.22, 14.7) * mm, "end": v(-38.84, 14.7) * mm});
            skLineSegment(sketch, "E338.trimOffspring", {"start": v(-38.72, 14.33) * mm, "end": v(-39.03, 14.1) * mm});
            skLineSegment(sketch, "E339.trimOffspring", {"start": v(-38.52, 14.47) * mm, "end": v(-38.4, 14.1) * mm});
            skLineSegment(sketch, "E340.trimOffspring", {"start": v(-38.6, 14.7) * mm, "end": v(-38.2, 14.7) * mm});
            skLineSegment(sketch, "E341.trimOffspring", {"start": v(-38.72, 14.33) * mm, "end": v(-38.4, 14.1) * mm});
            skLineSegment(sketch, "E342.trimOffspring", {"start": v(-38.84, 14.7) * mm, "end": v(-38.72, 15.07) * mm});
            skLineSegment(sketch, "E343", {"start": v(-40.74, 18.63) * mm, "end": v(-40.42, 18.4) * mm});
            skLineSegment(sketch, "E344", {"start": v(-40.54, 18.03) * mm, "end": v(-40.42, 18.4) * mm});
            skLineSegment(sketch, "E345", {"start": v(-39.72, 18.63) * mm, "end": v(-40.04, 18.4) * mm});
            skLineSegment(sketch, "E346", {"start": v(-40.23, 19) * mm, "end": v(-40.1, 18.63) * mm});
            skLineSegment(sketch, "E347", {"start": v(-40.74, 18.63) * mm, "end": v(-40.35, 18.63) * mm});
            skLineSegment(sketch, "E348.trimOffspring", {"start": v(-40.23, 18.26) * mm, "end": v(-40.54, 18.03) * mm});
            skLineSegment(sketch, "E349.trimOffspring", {"start": v(-40.04, 18.4) * mm, "end": v(-39.92, 18.03) * mm});
            skLineSegment(sketch, "E350.trimOffspring", {"start": v(-40.1, 18.63) * mm, "end": v(-39.72, 18.63) * mm});
            skLineSegment(sketch, "E351.trimOffspring", {"start": v(-40.23, 18.26) * mm, "end": v(-39.92, 18.03) * mm});
            skLineSegment(sketch, "E352.trimOffspring", {"start": v(-40.35, 18.63) * mm, "end": v(-40.23, 19) * mm});
            skLineSegment(sketch, "E353", {"start": v(-42.36, 17.33) * mm, "end": v(-42.05, 17.1) * mm});
            skLineSegment(sketch, "E354", {"start": v(-42.17, 16.73) * mm, "end": v(-42.05, 17.1) * mm});
            skLineSegment(sketch, "E355", {"start": v(-41.35, 17.33) * mm, "end": v(-41.66, 17.1) * mm});
            skLineSegment(sketch, "E356", {"start": v(-41.86, 17.7) * mm, "end": v(-41.74, 17.33) * mm});
            skLineSegment(sketch, "E357", {"start": v(-42.36, 17.33) * mm, "end": v(-41.98, 17.33) * mm});
            skLineSegment(sketch, "E358.trimOffspring", {"start": v(-41.86, 16.96) * mm, "end": v(-42.17, 16.73) * mm});
            skLineSegment(sketch, "E359.trimOffspring", {"start": v(-41.66, 17.1) * mm, "end": v(-41.54, 16.73) * mm});
            skLineSegment(sketch, "E360.trimOffspring", {"start": v(-41.74, 17.33) * mm, "end": v(-41.35, 17.33) * mm});
            skLineSegment(sketch, "E361.trimOffspring", {"start": v(-41.86, 16.96) * mm, "end": v(-41.54, 16.73) * mm});
            skLineSegment(sketch, "E362.trimOffspring", {"start": v(-41.98, 17.33) * mm, "end": v(-41.86, 17.7) * mm});
            skLineSegment(sketch, "E363", {"start": v(-43.97, 16.07) * mm, "end": v(-43.66, 15.84) * mm});
            skLineSegment(sketch, "E364", {"start": v(-43.78, 15.47) * mm, "end": v(-43.66, 15.84) * mm});
            skLineSegment(sketch, "E365", {"start": v(-42.96, 16.07) * mm, "end": v(-43.27, 15.84) * mm});
            skLineSegment(sketch, "E366", {"start": v(-43.46, 16.44) * mm, "end": v(-43.34, 16.07) * mm});
            skLineSegment(sketch, "E367", {"start": v(-43.97, 16.07) * mm, "end": v(-43.58, 16.07) * mm});
            skLineSegment(sketch, "E368.trimOffspring", {"start": v(-43.46, 15.7) * mm, "end": v(-43.78, 15.47) * mm});
            skLineSegment(sketch, "E369.trimOffspring", {"start": v(-43.27, 15.84) * mm, "end": v(-43.15, 15.47) * mm});
            skLineSegment(sketch, "E370.trimOffspring", {"start": v(-43.34, 16.07) * mm, "end": v(-42.96, 16.07) * mm});
            skLineSegment(sketch, "E371.trimOffspring", {"start": v(-43.46, 15.7) * mm, "end": v(-43.15, 15.47) * mm});
            skLineSegment(sketch, "E372.trimOffspring", {"start": v(-43.58, 16.07) * mm, "end": v(-43.46, 16.44) * mm});
            skLineSegment(sketch, "E373", {"start": v(-45.6, 14.56) * mm, "end": v(-45.29, 14.33) * mm});
            skLineSegment(sketch, "E374", {"start": v(-45.4, 13.96) * mm, "end": v(-45.29, 14.33) * mm});
            skLineSegment(sketch, "E375", {"start": v(-44.58, 14.56) * mm, "end": v(-44.9, 14.33) * mm});
            skLineSegment(sketch, "E376", {"start": v(-45.1, 14.93) * mm, "end": v(-44.97, 14.56) * mm});
            skLineSegment(sketch, "E377", {"start": v(-45.6, 14.56) * mm, "end": v(-45.21, 14.56) * mm});
            skLineSegment(sketch, "E378.trimOffspring", {"start": v(-45.1, 14.19) * mm, "end": v(-45.4, 13.96) * mm});
            skLineSegment(sketch, "E379.trimOffspring", {"start": v(-44.9, 14.33) * mm, "end": v(-44.78, 13.96) * mm});
            skLineSegment(sketch, "E380.trimOffspring", {"start": v(-44.97, 14.56) * mm, "end": v(-44.58, 14.56) * mm});
            skLineSegment(sketch, "E381.trimOffspring", {"start": v(-45.1, 14.19) * mm, "end": v(-44.78, 13.96) * mm});
            skLineSegment(sketch, "E382.trimOffspring", {"start": v(-45.21, 14.56) * mm, "end": v(-45.1, 14.93) * mm});
            skLineSegment(sketch, "E383", {"start": v(-42.43, 14.6) * mm, "end": v(-42.12, 14.38) * mm});
            skLineSegment(sketch, "E384", {"start": v(-42.24, 14) * mm, "end": v(-42.12, 14.38) * mm});
            skLineSegment(sketch, "E385", {"start": v(-41.42, 14.6) * mm, "end": v(-41.73, 14.38) * mm});
            skLineSegment(sketch, "E386", {"start": v(-41.93, 14.97) * mm, "end": v(-41.8, 14.6) * mm});
            skLineSegment(sketch, "E387", {"start": v(-42.43, 14.6) * mm, "end": v(-42.05, 14.6) * mm});
            skLineSegment(sketch, "E388.trimOffspring", {"start": v(-41.93, 14.24) * mm, "end": v(-42.24, 14) * mm});
            skLineSegment(sketch, "E389.trimOffspring", {"start": v(-41.73, 14.38) * mm, "end": v(-41.61, 14) * mm});
            skLineSegment(sketch, "E390.trimOffspring", {"start": v(-41.8, 14.6) * mm, "end": v(-41.42, 14.6) * mm});
            skLineSegment(sketch, "E391.trimOffspring", {"start": v(-41.93, 14.24) * mm, "end": v(-41.61, 14) * mm});
            skLineSegment(sketch, "E392.trimOffspring", {"start": v(-42.05, 14.6) * mm, "end": v(-41.93, 14.97) * mm});
            skLineSegment(sketch, "E393", {"start": v(-40.76, 16.07) * mm, "end": v(-40.45, 15.84) * mm});
            skLineSegment(sketch, "E394", {"start": v(-40.57, 15.47) * mm, "end": v(-40.45, 15.84) * mm});
            skLineSegment(sketch, "E395", {"start": v(-39.75, 16.07) * mm, "end": v(-40.06, 15.84) * mm});
            skLineSegment(sketch, "E396", {"start": v(-40.25, 16.44) * mm, "end": v(-40.13, 16.07) * mm});
            skLineSegment(sketch, "E397", {"start": v(-40.76, 16.07) * mm, "end": v(-40.37, 16.07) * mm});
            skLineSegment(sketch, "E398.trimOffspring", {"start": v(-40.25, 15.7) * mm, "end": v(-40.57, 15.47) * mm});
            skLineSegment(sketch, "E399.trimOffspring", {"start": v(-40.06, 15.84) * mm, "end": v(-39.94, 15.47) * mm});
            skLineSegment(sketch, "E400.trimOffspring", {"start": v(-40.13, 16.07) * mm, "end": v(-39.75, 16.07) * mm});
            skLineSegment(sketch, "E401.trimOffspring", {"start": v(-40.25, 15.7) * mm, "end": v(-39.94, 15.47) * mm});
            skLineSegment(sketch, "E402.trimOffspring", {"start": v(-40.37, 16.07) * mm, "end": v(-40.25, 16.44) * mm});
            skLineSegment(sketch, "E403", {"start": v(-37.55, 18.72) * mm, "end": v(-37.24, 18.5) * mm});
            skLineSegment(sketch, "E404", {"start": v(-37.36, 18.13) * mm, "end": v(-37.24, 18.5) * mm});
            skLineSegment(sketch, "E405", {"start": v(-36.53, 18.72) * mm, "end": v(-36.85, 18.5) * mm});
            skLineSegment(sketch, "E406", {"start": v(-37.04, 19.1) * mm, "end": v(-36.92, 18.72) * mm});
            skLineSegment(sketch, "E407", {"start": v(-37.55, 18.72) * mm, "end": v(-37.16, 18.72) * mm});
            skLineSegment(sketch, "E408.trimOffspring", {"start": v(-37.04, 18.35) * mm, "end": v(-37.36, 18.13) * mm});
            skLineSegment(sketch, "E409.trimOffspring", {"start": v(-36.85, 18.5) * mm, "end": v(-36.73, 18.13) * mm});
            skLineSegment(sketch, "E410.trimOffspring", {"start": v(-36.92, 18.72) * mm, "end": v(-36.53, 18.72) * mm});
            skLineSegment(sketch, "E411.trimOffspring", {"start": v(-37.04, 18.35) * mm, "end": v(-36.73, 18.13) * mm});
            skLineSegment(sketch, "E412.trimOffspring", {"start": v(-37.16, 18.72) * mm, "end": v(-37.04, 19.1) * mm});
            skLineSegment(sketch, "E413", {"start": v(-37.6, 16.07) * mm, "end": v(-37.28, 15.84) * mm});
            skLineSegment(sketch, "E414", {"start": v(-37.4, 15.47) * mm, "end": v(-37.28, 15.84) * mm});
            skLineSegment(sketch, "E415", {"start": v(-36.58, 16.07) * mm, "end": v(-36.9, 15.84) * mm});
            skLineSegment(sketch, "E416", {"start": v(-37.09, 16.44) * mm, "end": v(-36.97, 16.07) * mm});
            skLineSegment(sketch, "E417", {"start": v(-37.6, 16.07) * mm, "end": v(-37.2, 16.07) * mm});
            skLineSegment(sketch, "E418.trimOffspring", {"start": v(-37.09, 15.7) * mm, "end": v(-37.4, 15.47) * mm});
            skLineSegment(sketch, "E419.trimOffspring", {"start": v(-36.9, 15.84) * mm, "end": v(-36.78, 15.47) * mm});
            skLineSegment(sketch, "E420.trimOffspring", {"start": v(-36.97, 16.07) * mm, "end": v(-36.58, 16.07) * mm});
            skLineSegment(sketch, "E421.trimOffspring", {"start": v(-37.09, 15.7) * mm, "end": v(-36.78, 15.47) * mm});
            skLineSegment(sketch, "E422.trimOffspring", {"start": v(-37.2, 16.07) * mm, "end": v(-37.09, 16.44) * mm});
            skLineSegment(sketch, "E423", {"start": v(-35.97, 17.37) * mm, "end": v(-35.65, 17.14) * mm});
            skLineSegment(sketch, "E424", {"start": v(-35.77, 16.78) * mm, "end": v(-35.65, 17.14) * mm});
            skLineSegment(sketch, "E425", {"start": v(-34.95, 17.37) * mm, "end": v(-35.27, 17.14) * mm});
            skLineSegment(sketch, "E426", {"start": v(-35.46, 17.74) * mm, "end": v(-35.34, 17.37) * mm});
            skLineSegment(sketch, "E427", {"start": v(-35.97, 17.37) * mm, "end": v(-35.58, 17.37) * mm});
            skLineSegment(sketch, "E428.trimOffspring", {"start": v(-35.46, 17) * mm, "end": v(-35.77, 16.78) * mm});
            skLineSegment(sketch, "E429.trimOffspring", {"start": v(-35.27, 17.14) * mm, "end": v(-35.15, 16.78) * mm});
            skLineSegment(sketch, "E430.trimOffspring", {"start": v(-35.34, 17.37) * mm, "end": v(-34.95, 17.37) * mm});
            skLineSegment(sketch, "E431.trimOffspring", {"start": v(-35.46, 17) * mm, "end": v(-35.15, 16.78) * mm});
            skLineSegment(sketch, "E432.trimOffspring", {"start": v(-35.58, 17.37) * mm, "end": v(-35.46, 17.74) * mm});
            skLineSegment(sketch, "E433", {"start": v(-34.43, 16.02) * mm, "end": v(-34.12, 15.8) * mm});
            skLineSegment(sketch, "E434", {"start": v(-34.24, 15.43) * mm, "end": v(-34.12, 15.8) * mm});
            skLineSegment(sketch, "E435", {"start": v(-33.42, 16.02) * mm, "end": v(-33.73, 15.8) * mm});
            skLineSegment(sketch, "E436", {"start": v(-33.92, 16.4) * mm, "end": v(-33.8, 16.02) * mm});
            skLineSegment(sketch, "E437", {"start": v(-34.43, 16.02) * mm, "end": v(-34.04, 16.02) * mm});
            skLineSegment(sketch, "E438.trimOffspring", {"start": v(-33.92, 15.65) * mm, "end": v(-34.24, 15.43) * mm});
            skLineSegment(sketch, "E439.trimOffspring", {"start": v(-33.73, 15.8) * mm, "end": v(-33.61, 15.43) * mm});
            skLineSegment(sketch, "E440.trimOffspring", {"start": v(-33.8, 16.02) * mm, "end": v(-33.42, 16.02) * mm});
            skLineSegment(sketch, "E441.trimOffspring", {"start": v(-33.92, 15.65) * mm, "end": v(-33.61, 15.43) * mm});
            skLineSegment(sketch, "E442.trimOffspring", {"start": v(-34.04, 16.02) * mm, "end": v(-33.92, 16.4) * mm});
            skLineSegment(sketch, "E443", {"start": v(-35.97, 14.65) * mm, "end": v(-35.65, 14.42) * mm});
            skLineSegment(sketch, "E444", {"start": v(-35.77, 14.05) * mm, "end": v(-35.65, 14.42) * mm});
            skLineSegment(sketch, "E445", {"start": v(-34.95, 14.65) * mm, "end": v(-35.27, 14.42) * mm});
            skLineSegment(sketch, "E446", {"start": v(-35.46, 15.02) * mm, "end": v(-35.34, 14.65) * mm});
            skLineSegment(sketch, "E447", {"start": v(-35.97, 14.65) * mm, "end": v(-35.58, 14.65) * mm});
            skLineSegment(sketch, "E448.trimOffspring", {"start": v(-35.46, 14.28) * mm, "end": v(-35.77, 14.05) * mm});
            skLineSegment(sketch, "E449.trimOffspring", {"start": v(-35.27, 14.42) * mm, "end": v(-35.15, 14.05) * mm});
            skLineSegment(sketch, "E450.trimOffspring", {"start": v(-35.34, 14.65) * mm, "end": v(-34.95, 14.65) * mm});
            skLineSegment(sketch, "E451.trimOffspring", {"start": v(-35.46, 14.28) * mm, "end": v(-35.15, 14.05) * mm});
            skLineSegment(sketch, "E452.trimOffspring", {"start": v(-35.58, 14.65) * mm, "end": v(-35.46, 15.02) * mm});
            skLineSegment(sketch, "E453", {"start": v(-32.78, 14.65) * mm, "end": v(-32.47, 14.42) * mm});
            skLineSegment(sketch, "E454", {"start": v(-32.59, 14.05) * mm, "end": v(-32.47, 14.42) * mm});
            skLineSegment(sketch, "E455", {"start": v(-31.77, 14.65) * mm, "end": v(-32.08, 14.42) * mm});
            skLineSegment(sketch, "E456", {"start": v(-32.27, 15.02) * mm, "end": v(-32.15, 14.65) * mm});
            skLineSegment(sketch, "E457", {"start": v(-32.78, 14.65) * mm, "end": v(-32.4, 14.65) * mm});
            skLineSegment(sketch, "E458.trimOffspring", {"start": v(-32.27, 14.28) * mm, "end": v(-32.59, 14.05) * mm});
            skLineSegment(sketch, "E459.trimOffspring", {"start": v(-32.08, 14.42) * mm, "end": v(-31.96, 14.05) * mm});
            skLineSegment(sketch, "E460.trimOffspring", {"start": v(-32.15, 14.65) * mm, "end": v(-31.77, 14.65) * mm});
            skLineSegment(sketch, "E461.trimOffspring", {"start": v(-32.27, 14.28) * mm, "end": v(-31.96, 14.05) * mm});
            skLineSegment(sketch, "E462.trimOffspring", {"start": v(-32.4, 14.65) * mm, "end": v(-32.27, 15.02) * mm});
            skLineSegment(sketch, "E463", {"start": v(-47.17, 13.25) * mm, "end": v(-46.85, 13.02) * mm});
            skLineSegment(sketch, "E464", {"start": v(-46.97, 12.65) * mm, "end": v(-46.85, 13.02) * mm});
            skLineSegment(sketch, "E465", {"start": v(-46.15, 13.25) * mm, "end": v(-46.47, 13.02) * mm});
            skLineSegment(sketch, "E466", {"start": v(-46.66, 13.62) * mm, "end": v(-46.54, 13.25) * mm});
            skLineSegment(sketch, "E467", {"start": v(-47.17, 13.25) * mm, "end": v(-46.78, 13.25) * mm});
            skLineSegment(sketch, "E468.trimOffspring", {"start": v(-46.66, 12.88) * mm, "end": v(-46.97, 12.65) * mm});
            skLineSegment(sketch, "E469.trimOffspring", {"start": v(-46.47, 13.02) * mm, "end": v(-46.35, 12.65) * mm});
            skLineSegment(sketch, "E470.trimOffspring", {"start": v(-46.54, 13.25) * mm, "end": v(-46.15, 13.25) * mm});
            skLineSegment(sketch, "E471.trimOffspring", {"start": v(-46.66, 12.88) * mm, "end": v(-46.35, 12.65) * mm});
            skLineSegment(sketch, "E472.trimOffspring", {"start": v(-46.78, 13.25) * mm, "end": v(-46.66, 13.62) * mm});
            skLineSegment(sketch, "E473", {"start": v(-43.98, 13.26) * mm, "end": v(-43.66, 13.04) * mm});
            skLineSegment(sketch, "E474", {"start": v(-43.78, 12.67) * mm, "end": v(-43.66, 13.04) * mm});
            skLineSegment(sketch, "E475", {"start": v(-42.96, 13.26) * mm, "end": v(-43.28, 13.04) * mm});
            skLineSegment(sketch, "E476", {"start": v(-43.47, 13.63) * mm, "end": v(-43.35, 13.26) * mm});
            skLineSegment(sketch, "E477", {"start": v(-43.98, 13.26) * mm, "end": v(-43.59, 13.26) * mm});
            skLineSegment(sketch, "E478.trimOffspring", {"start": v(-43.47, 12.9) * mm, "end": v(-43.78, 12.67) * mm});
            skLineSegment(sketch, "E479.trimOffspring", {"start": v(-43.28, 13.04) * mm, "end": v(-43.16, 12.67) * mm});
            skLineSegment(sketch, "E480.trimOffspring", {"start": v(-43.35, 13.26) * mm, "end": v(-42.96, 13.26) * mm});
            skLineSegment(sketch, "E481.trimOffspring", {"start": v(-43.47, 12.9) * mm, "end": v(-43.16, 12.67) * mm});
            skLineSegment(sketch, "E482.trimOffspring", {"start": v(-43.59, 13.26) * mm, "end": v(-43.47, 13.63) * mm});
            skLineSegment(sketch, "E483", {"start": v(-40.75, 13.26) * mm, "end": v(-40.44, 13.04) * mm});
            skLineSegment(sketch, "E484", {"start": v(-40.56, 12.67) * mm, "end": v(-40.44, 13.04) * mm});
            skLineSegment(sketch, "E485", {"start": v(-39.74, 13.26) * mm, "end": v(-40.05, 13.04) * mm});
            skLineSegment(sketch, "E486", {"start": v(-40.25, 13.63) * mm, "end": v(-40.13, 13.26) * mm});
            skLineSegment(sketch, "E487", {"start": v(-40.75, 13.26) * mm, "end": v(-40.37, 13.26) * mm});
            skLineSegment(sketch, "E488.trimOffspring", {"start": v(-40.25, 12.9) * mm, "end": v(-40.56, 12.67) * mm});
            skLineSegment(sketch, "E489.trimOffspring", {"start": v(-40.05, 13.04) * mm, "end": v(-39.93, 12.67) * mm});
            skLineSegment(sketch, "E490.trimOffspring", {"start": v(-40.13, 13.26) * mm, "end": v(-39.74, 13.26) * mm});
            skLineSegment(sketch, "E491.trimOffspring", {"start": v(-40.25, 12.9) * mm, "end": v(-39.93, 12.67) * mm});
            skLineSegment(sketch, "E492.trimOffspring", {"start": v(-40.37, 13.26) * mm, "end": v(-40.25, 13.63) * mm});
            skLineSegment(sketch, "E493", {"start": v(-37.6, 13.26) * mm, "end": v(-37.28, 13.04) * mm});
            skLineSegment(sketch, "E494", {"start": v(-37.4, 12.67) * mm, "end": v(-37.28, 13.04) * mm});
            skLineSegment(sketch, "E495", {"start": v(-36.58, 13.26) * mm, "end": v(-36.9, 13.04) * mm});
            skLineSegment(sketch, "E496", {"start": v(-37.09, 13.63) * mm, "end": v(-36.97, 13.26) * mm});
            skLineSegment(sketch, "E497", {"start": v(-37.6, 13.26) * mm, "end": v(-37.2, 13.26) * mm});
            skLineSegment(sketch, "E498.trimOffspring", {"start": v(-37.09, 12.9) * mm, "end": v(-37.4, 12.67) * mm});
            skLineSegment(sketch, "E499.trimOffspring", {"start": v(-36.9, 13.04) * mm, "end": v(-36.77, 12.67) * mm});
            skLineSegment(sketch, "E500.trimOffspring", {"start": v(-36.97, 13.26) * mm, "end": v(-36.58, 13.26) * mm});
            skLineSegment(sketch, "E501.trimOffspring", {"start": v(-37.09, 12.9) * mm, "end": v(-36.77, 12.67) * mm});
            skLineSegment(sketch, "E502.trimOffspring", {"start": v(-37.2, 13.26) * mm, "end": v(-37.09, 13.63) * mm});
            skLineSegment(sketch, "E503", {"start": v(-34.35, 13.28) * mm, "end": v(-34.04, 13.05) * mm});
            skLineSegment(sketch, "E504", {"start": v(-34.16, 12.68) * mm, "end": v(-34.04, 13.05) * mm});
            skLineSegment(sketch, "E505", {"start": v(-33.34, 13.28) * mm, "end": v(-33.65, 13.05) * mm});
            skLineSegment(sketch, "E506", {"start": v(-33.85, 13.65) * mm, "end": v(-33.73, 13.28) * mm});
            skLineSegment(sketch, "E507", {"start": v(-34.35, 13.28) * mm, "end": v(-33.97, 13.28) * mm});
            skLineSegment(sketch, "E508.trimOffspring", {"start": v(-33.85, 12.91) * mm, "end": v(-34.16, 12.68) * mm});
            skLineSegment(sketch, "E509.trimOffspring", {"start": v(-33.65, 13.05) * mm, "end": v(-33.53, 12.68) * mm});
            skLineSegment(sketch, "E510.trimOffspring", {"start": v(-33.73, 13.28) * mm, "end": v(-33.34, 13.28) * mm});
            skLineSegment(sketch, "E511.trimOffspring", {"start": v(-33.85, 12.91) * mm, "end": v(-33.53, 12.68) * mm});
            skLineSegment(sketch, "E512.trimOffspring", {"start": v(-33.97, 13.28) * mm, "end": v(-33.85, 13.65) * mm});
            skLineSegment(sketch, "E513", {"start": v(-31.03, 13.25) * mm, "end": v(-30.72, 13.02) * mm});
            skLineSegment(sketch, "E514", {"start": v(-30.84, 12.65) * mm, "end": v(-30.72, 13.02) * mm});
            skLineSegment(sketch, "E515", {"start": v(-30.02, 13.25) * mm, "end": v(-30.33, 13.02) * mm});
            skLineSegment(sketch, "E516", {"start": v(-30.52, 13.62) * mm, "end": v(-30.4, 13.25) * mm});
            skLineSegment(sketch, "E517", {"start": v(-31.03, 13.25) * mm, "end": v(-30.64, 13.25) * mm});
            skLineSegment(sketch, "E518.trimOffspring", {"start": v(-30.52, 12.88) * mm, "end": v(-30.84, 12.65) * mm});
            skLineSegment(sketch, "E519.trimOffspring", {"start": v(-30.33, 13.02) * mm, "end": v(-30.2, 12.65) * mm});
            skLineSegment(sketch, "E520.trimOffspring", {"start": v(-30.4, 13.25) * mm, "end": v(-30.02, 13.25) * mm});
            skLineSegment(sketch, "E521.trimOffspring", {"start": v(-30.52, 12.88) * mm, "end": v(-30.2, 12.65) * mm});
            skLineSegment(sketch, "E522.trimOffspring", {"start": v(-30.64, 13.25) * mm, "end": v(-30.52, 13.62) * mm});
            skLineSegment(sketch, "E523.trimOffspring", {"start": v(-46.66, 23.82) * mm, "end": v(-46.66, 24.56) * mm});
            skLineSegment(sketch, "E524.0", {"start": v(-28.96, 17.58) * mm, "end": v(0, 17.58) * mm});
            skLineSegment(sketch, "E525.0", {"start": v(-28.96, 15.63) * mm, "end": v(0, 15.63) * mm});
            skLineSegment(sketch, "E526.trimOffspring", {"start": v(-28.96, 11.7) * mm, "end": v(-28.96, 25.4) * mm});
            skSolve(sketch);
        }
        {
            var Q0;
            {var subQ14=sQuery(id+"F0.wireOp",EDGE,"E24");Q0=makeQuery(id+"F0.imprint","IMPRINT",FACE,{"disambiguationData":[TD([[makeQuery(id+"F0.imprint","IMPRINT",EDGE,{"derivedFrom":subQ14}),1.0]])]});}
            extrude(context, id + "F1", {"entities" : qUnion([Q0]), "depth" : 25.4 * mm, "offsetDistance" : 25.4 * mm});
        }
    });
